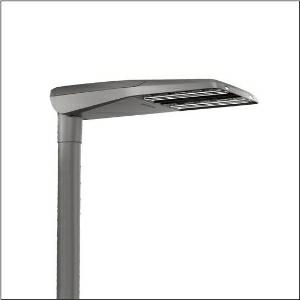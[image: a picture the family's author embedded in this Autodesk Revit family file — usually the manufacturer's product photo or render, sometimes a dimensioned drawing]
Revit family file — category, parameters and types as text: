
# Revit family: streetlight_sl_11_iq_midi___st1_2a_5xc3a61g08me_c756
name_source: partatom
category: Lighting Fixtures
units: mm (PartAtom-declared; Revit-internal decimal feet)

## family parameters
Cut with Voids When Loaded = No
Host = Face
Light Source = No
Part Type = Normal
Room Calculation Point = No
Round Connector Dimension = Use Diameter
Shared = No

## types (1)
- --- (1 x LED, 16120 lm, 123.9 W, 2700K)
    Apparent Load = 124 VA
    CIE Flux Codes = 32 70 96 100 100
    Color Rendering = 70
    Color Temperature = 2700K
    Default Elevation = 1800 mm
    Description = Streetlight SL 11 iQ midi, mast luminaire, primary light control with 3 zone facetted reflector, of plastic, silver coated, highly specular, primary optical cover: cover, of PMMA, transparent, light distribution: ST1.2a, light emission: direct distribution, primary light characteristic: asymmetric, installation type: post-top, side-entry, lamps: LED, High Power LED, rated values: 16.120lm | 123,9W | 130,1lm/W (begin service life); end service life: 16.120lm | 130,9W; at 50% lumin. flux: 8.060lm | 56,7W | 142,2lm/W, colour temperature: 2700K, colour rendering: CRI > 70, light colour: 727, light setting 1 begin service life: 100% | 16.120lm | 123,9W | 130,1lm/W | 2.700K, light setting 1 end service life: 130,9W, further light settings possible, control: Street-Remote, Auto-Match, Temp-Guard, Lumen-Switch, Night-Set, Smart-Wire, Light-Fading, Desk-Remote (wireless, voltage-free reading and setting of iQ features in the workshop via application-optimized NFC function/RFID function), optimised constant luminous flux control (CLO 2.0), pre-setting: linear dimming characteristic, with cable H07RN-F 5x 1.5mm², mains connection: 230..240V, AC, 50/60Hz, connection cable pre-assembled, cable length: 12,5m, luminaire housing, of diecast aluminium, powder-coated, Siteco® metallic grey (DB 702S), please order mast flange separately, inclination adjustable without tools: 0°, 5°, 10°, 15° (post-top) | 0°, -5°, -10°, -15° (side-entry), sealing non-destructively replaceable, multi-level sealing system, length: 780mm, width: 376mm, height: 118mm, mast flange for spigot size: 42mm (side-entry): 5XC10008XM4, 60/48mm (side-entry/post-top): 5XC10108XM2, 76/60mm (side-entry/post-top): 5XC10108XM1, equipment: Power, protection rating (complete): IP66, insulation class (complete): insulation class II (safety insulation), certification: CE, ENEC, ENEC+, VDE, impact resistance: IK10, permissible operating ambient temperature for outdoor applications: -25..+50°C, standard-compliant lighting for roads and squares, Environmental Product Declaration (EPD) tested and certified by an independent institute, packaging unit: 1 piece

Light Distribution: ST1.2a
    Height = 118 mm
    Lamp = 1 x LED
    Lamp Light Flux = 16120 lm
    Lamp Power = 123.9 W
    Lamp count = 1
    Length = 780 mm
    Luminous efficacy = 130 lm/W
    Manufacturer = Siteco
    ModVariant = No
    Model = 5XC3A61G08ME
    Number of Poles = 1
    OnlyDefault = Yes
    Power Factor = 1
    Product Name = Streetlight SL 11 iQ midi | ST1.2a
    Product group = mast luminaire | pylon top
    ProductGroupID = 6100
    Protection Class = Protection class II
    Protection Degree = IP 66
    RLX_Detail_Level = 1
    RLX_Emergency_Light_Flux = 0 lm
    RLX_Emergency_Type = 0
    RLX_Emergency_Type_DB = No
    RlxData = <blob elided: 70985 chars, md5=520f6593>
    Socket = socket
    Standby Power = 0 W
    System Light Flux = 16119 lm
    System Power = 124 W
    Type Comments = factory setting: luminous flux: 100 % | dim-lin: 254 | 554 mA
    Type Image = l_1005960.jpg
    URL = http://relux.com
    VarID = @adj_099781
    Voltage = 0 V
    Weight = 0.00 kg
    Width = 376 mm

## geometry (parser evidence)
native form markers: Blend x4, Sweep x10
no freeform markers — native parametric forms only
